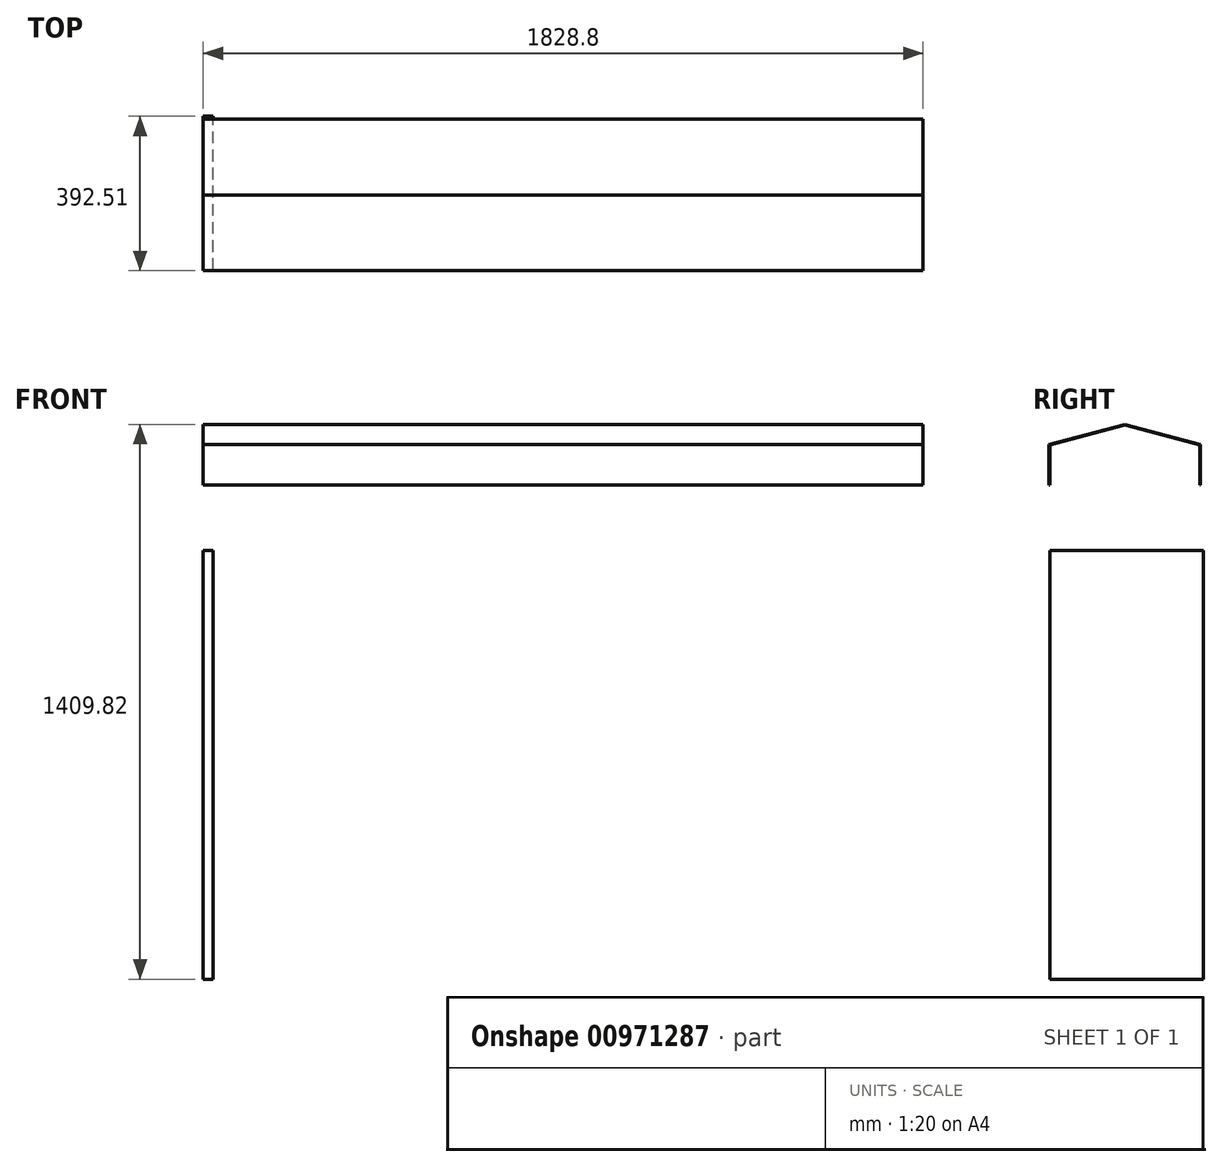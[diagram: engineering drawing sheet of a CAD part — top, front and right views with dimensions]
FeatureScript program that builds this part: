
annotation { "Feature Type Name" : "Feature", "Feature Type Description" : "" }
export const myFeature = defineFeature(function(context is Context, id is Id, definition is map)
    precondition{}
    {
        {
            var Q0;
            Q0=qCreatedBy(makeId("Right.planeOp"),FACE);
            var sketch = newSketch(context, id + "F0", { "sketchPlane" : qUnion([Q0])});
            skLineSegment(sketch, "E0", {"start": v(190.5, 50.8) * mm, "end": v(0, 0) * mm});
            skLineSegment(sketch, "E1", {"start": v(190.5, 50.8) * mm, "end": v(381, 0) * mm});
            skLineSegment(sketch, "E2", {"start": v(381, 0) * mm, "end": v(381, -101.6) * mm});
            skLineSegment(sketch, "E3", {"start": v(0, 0) * mm, "end": v(0, -101.6) * mm});
            skLineSegment(sketch, "E4.0", {"start": v(-1.98, 1.52) * mm, "end": v(-1.98, -101.6) * mm});
            skLineSegment(sketch, "E4.1", {"start": v(190.5, 52.85) * mm, "end": v(-1.98, 1.52) * mm});
            skLineSegment(sketch, "E4.2", {"start": v(190.5, 52.85) * mm, "end": v(382.98, 1.52) * mm});
            skLineSegment(sketch, "E4.3", {"start": v(382.98, 1.52) * mm, "end": v(382.98, -101.6) * mm});
            skLineSegment(sketch, "E5", {"start": v(-1.98, -101.6) * mm, "end": v(0, -101.6) * mm});
            skLineSegment(sketch, "E6", {"start": v(381, -101.6) * mm, "end": v(382.98, -101.6) * mm});
            skLineSegment(sketch, "E7", {"start": v(0, -267.25) * mm, "end": v(0, -1486.45) * mm});
            skLineSegment(sketch, "E8", {"start": v(0, -267.25) * mm, "end": v(390.53, -267.25) * mm});
            skLineSegment(sketch, "E9", {"start": v(390.53, -267.25) * mm, "end": v(390.52, -1486.45) * mm});
            skLineSegment(sketch, "E10", {"start": v(0, -1486.45) * mm, "end": v(48.98, -1544.82) * mm});
            skLineSegment(sketch, "E11", {"start": v(390.52, -1486.45) * mm, "end": v(341.54, -1544.82) * mm});
            skLineSegment(sketch, "E12", {"start": v(0, -876.85) * mm, "end": v(390.52, -876.85) * mm});
            skLineSegment(sketch, "E13", {"start": v(0, -1356.97) * mm, "end": v(390.53, -1356.97) * mm});
            skSolve(sketch);
        }
        {
            var Q0;
            Q0=makeQuery(id+"F0.imprint","IMPRINT",FACE,{"disambiguationData":[TD([[makeQuery(id+"F0.imprint","IMPRINT",EDGE,{"derivedFrom":sQuery(id+"F0.wireOp",EDGE,"E0")}),-1.0]])]});
            extrude(context, id + "F1", {"entities" : qUnion([Q0]), "depth" : 1828.8 * mm, "offsetDistance" : 25.4 * mm});
        }
        {
            var Q0;
            Q0 = qSketchRegion(id + "F0", true);
            extrude(context, id + "F2", {"entities" : qUnion([Q0]), "operationType" : NewBodyOperationType.ADD, "depth" : 25.4 * mm, "offsetDistance" : 25.4 * mm});
        }
    });
